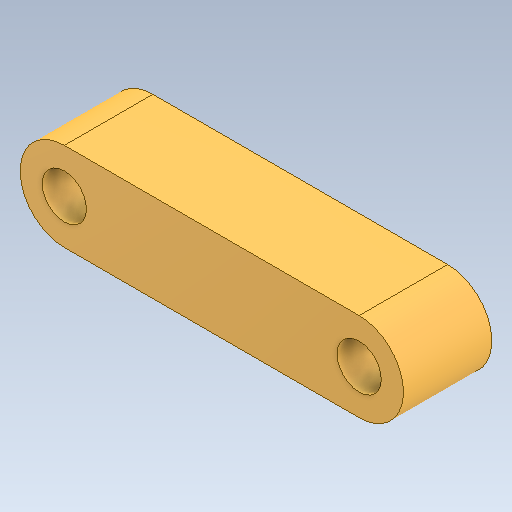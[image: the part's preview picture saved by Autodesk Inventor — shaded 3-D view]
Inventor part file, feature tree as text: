
AUTODESK INVENTOR PART (.ipt)
format: ipt  version: 2021.4 (Build 254397000, 397)  size: 102,912 bytes
history: imported  units: in
note: dims shown in document units (in); Inventor stores cm internally (conversion verified against a paired STEP export)
features: imported_body x1
ambient origin geometry x8: Origin, YZ Plane, XZ Plane, XY Plane, X Axis, Y Axis, Z Axis, Center Point
bodies: Solid1 (imported_parasolid), Body1 (imported_parasolid)
feature tree (1):
  imported_body  NMx_Import_Brep_tag  [imported B-rep: ~8 faces, bbox_mm=[1000.0, 300.0, 300.0]]
